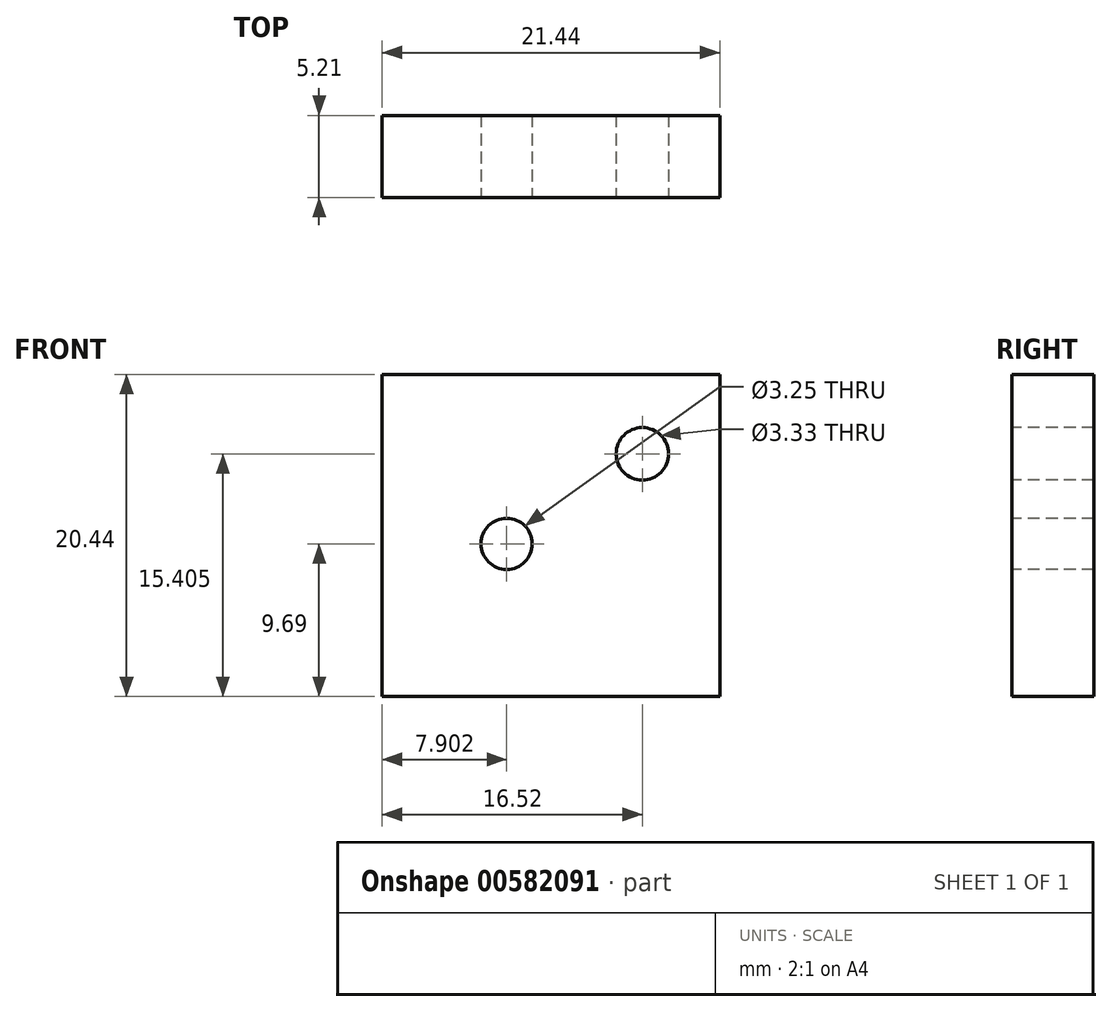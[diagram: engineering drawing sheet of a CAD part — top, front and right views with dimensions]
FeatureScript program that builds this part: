
annotation { "Feature Type Name" : "Feature", "Feature Type Description" : "" }
export const myFeature = defineFeature(function(context is Context, id is Id, definition is map)
    precondition{}
    {
        {
            var Q0;
            Q0=qCreatedBy(makeId("Front.planeOp"),FACE);
            var sketch = newSketch(context, id + "F0", { "sketchPlane" : qUnion([Q0])});
            skLineSegment(sketch, "E0.bottom", {"start": v(10.72, -10.22) * mm, "end": v(-10.72, -10.22) * mm});
            skLineSegment(sketch, "E0.top", {"start": v(10.72, 10.23) * mm, "end": v(-10.72, 10.22) * mm});
            skLineSegment(sketch, "E0.left", {"start": v(10.72, -10.22) * mm, "end": v(10.72, 10.23) * mm});
            skLineSegment(sketch, "E0.right", {"start": v(-10.72, -10.22) * mm, "end": v(-10.72, 10.22) * mm});
            skPoint(sketch, "E0.middle", {"position": v(0, 0) * mm});
            skSolve(sketch);
        }
        {
            var Q0;
            Q0 = qSketchRegion(id + "F0", true);
            extrude(context, id + "F1", {"entities" : qUnion([Q0]), "depth" : 5.2 * mm, "offsetDistance" : 25 * mm});
        }
        {
            var Q0;
            Q0=makeQuery(id+"F1.opExtrude","CAP_FACE",FACE,{"disambiguationData":[OSD([sQuery(id+"F0.wireOp",EDGE,"E0.bottom"),sQuery(id+"F0.wireOp",EDGE,"E0.top"),sQuery(id+"F0.wireOp",EDGE,"E0.left"),sQuery(id+"F0.wireOp",EDGE,"E0.right")])],"isStart":false});
            var sketch = newSketch(context, id + "F2", { "sketchPlane" : qUnion([Q0])});
            skCircle(sketch, "E1", {"center": v(5.8, 5.19) * mm, "radius": 1.67 * mm});
            skCircle(sketch, "E2", {"center": v(-2.82, -0.53) * mm, "radius": 1.63 * mm});
            skSolve(sketch);
        }
        {
            var Q0;
            Q0 = qSketchRegion(id + "F2", true);
            extrude(context, id + "F3", {"entities" : qUnion([Q0]), "operationType" : NewBodyOperationType.REMOVE, "endBound" : BoundingType.THROUGH_ALL, "oppositeDirection" : true, "depth" : 25 * mm, "offsetDistance" : 25 * mm});
        }
    });
